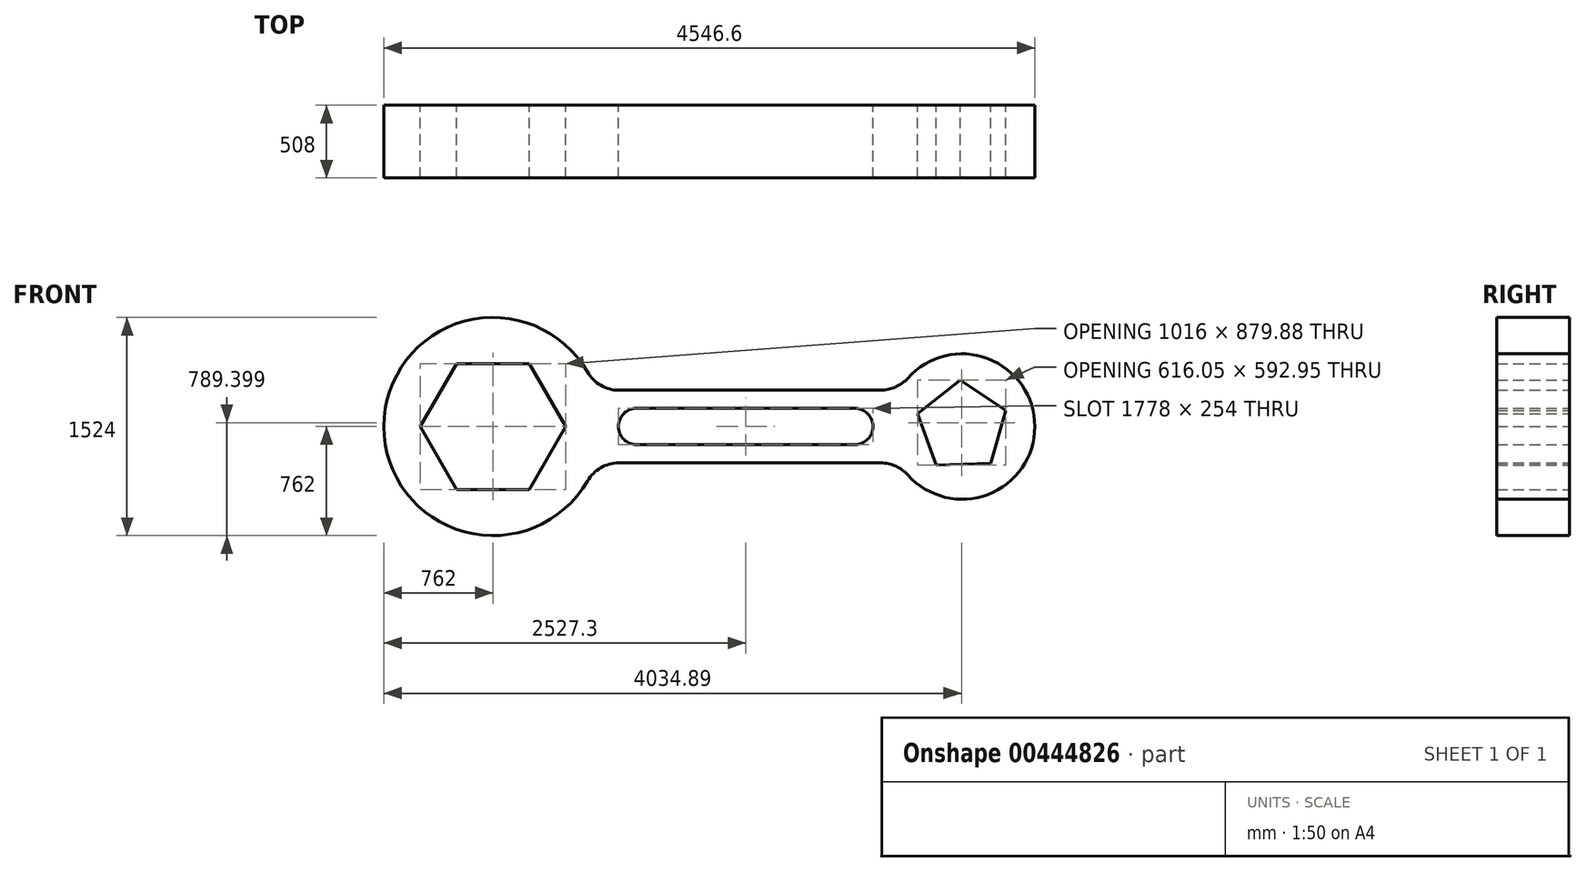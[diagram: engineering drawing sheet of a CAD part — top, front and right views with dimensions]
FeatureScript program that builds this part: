
annotation { "Feature Type Name" : "Feature", "Feature Type Description" : "" }
export const myFeature = defineFeature(function(context is Context, id is Id, definition is map)
    precondition{}
    {
        {
            var Q0;
            Q0=qCreatedBy(makeId("Front.planeOp"),FACE);
            var sketch = newSketch(context, id + "F0", { "sketchPlane" : qUnion([Q0])});
            skCircle(sketch, "E0", {"center": v(0, 0) * mm, "radius": 762 * mm});
            skLineSegment(sketch, "E1.0", {"start": v(-254, 439.94) * mm, "end": v(254, 439.94) * mm});
            skLineSegment(sketch, "E1.1", {"start": v(254, 439.94) * mm, "end": v(508, 0) * mm});
            skLineSegment(sketch, "E1.2", {"start": v(508, 0) * mm, "end": v(254, -439.94) * mm});
            skLineSegment(sketch, "E1.3", {"start": v(254, -439.94) * mm, "end": v(-254, -439.94) * mm});
            skLineSegment(sketch, "E1.4", {"start": v(-254, -439.94) * mm, "end": v(-508, 0) * mm});
            skLineSegment(sketch, "E1.5", {"start": v(-508, 0) * mm, "end": v(-254, 439.94) * mm});
            skPoint(sketch, "E1.0.midPoint", {"position": v(0, 439.94) * mm});
            skCircle(sketch, "E2", {"center": v(3276.6, 0) * mm, "radius": 508 * mm});
            skCircle(sketch, "E3.cCircle", {"center": v(3276.6, 0) * mm, "radius": 262.2 * mm, "construction": true});
            skLineSegment(sketch, "E3.0", {"start": v(2964.87, 88.67) * mm, "end": v(3264.6, 323.88) * mm});
            skLineSegment(sketch, "E3.1", {"start": v(3264.6, 323.88) * mm, "end": v(3580.91, 111.5) * mm});
            skLineSegment(sketch, "E3.2", {"start": v(3580.91, 111.5) * mm, "end": v(3476.68, -254.96) * mm});
            skLineSegment(sketch, "E3.3", {"start": v(3476.68, -254.96) * mm, "end": v(3095.94, -269.08) * mm});
            skLineSegment(sketch, "E3.4", {"start": v(3095.94, -269.08) * mm, "end": v(2964.87, 88.67) * mm});
            skPoint(sketch, "E3.0.midPoint", {"position": v(3114.73, 206.27) * mm});
            skLineSegment(sketch, "E4.0", {"start": v(876.3, 254) * mm, "end": v(2708.64, 254) * mm});
            skLineSegment(sketch, "E5.trimOffspring", {"start": v(2997.35, 0) * mm, "end": v(3276.6, 0) * mm});
            skLineSegment(sketch, "E6", {"start": v(1765.3, 0) * mm, "end": v(1765.3, 254) * mm});
            skArc(sketch, "E7", {"start": v(1003.3, 127) * mm, "mid": v(876.3, 0) * mm, "end": v(1003.3, -127) * mm});
            skArc(sketch, "E8", {"start": v(2527.3, -127) * mm, "mid": v(2654.3, 0) * mm, "end": v(2527.3, 127) * mm});
            skLineSegment(sketch, "E9", {"start": v(1003.3, 127) * mm, "end": v(2527.3, 127) * mm});
            skLineSegment(sketch, "E10", {"start": v(1003.3, -127) * mm, "end": v(2527.3, -127) * mm});
            skArc(sketch, "E11", {"start": v(879.88, -254) * mm, "mid": v(752.88, -288.03) * mm, "end": v(659.91, -381) * mm});
            skLineSegment(sketch, "E12.trimOffspring", {"start": v(879.88, -254) * mm, "end": v(2708.64, -254) * mm});
            skArc(sketch, "E13", {"start": v(659.91, 381) * mm, "mid": v(752.88, 288.03) * mm, "end": v(879.88, 254) * mm});
            skArc(sketch, "E14", {"start": v(2708.64, 254) * mm, "mid": v(2812.33, 276.13) * mm, "end": v(2897.96, 338.67) * mm});
            skArc(sketch, "E15", {"start": v(2897.96, -338.67) * mm, "mid": v(2812.33, -276.13) * mm, "end": v(2708.64, -254) * mm});
            skPoint(sketch, "E16.orphan", {"position": v(762, 0) * mm});
            skPoint(sketch, "E17.trimOffspring.end.orphan", {"position": v(2768.6, 0) * mm});
            skLineSegment(sketch, "E18.trimOffspring", {"start": v(3175.55, 254) * mm, "end": v(3276.6, 254) * mm});
            skLineSegment(sketch, "E19.trimOffspring", {"start": v(3090.42, -254) * mm, "end": v(3276.6, -254) * mm});
            skSolve(sketch);
        }
        {
            var Q0;
            Q0 = qSketchRegion(id + "F0", true);
            extrude(context, id + "F1", {"entities" : qUnion([Q0]), "depth" : 25.4 * mm});
        }
        {
            var Q0;
            Q0 = qSketchRegion(id + "F0", true);
            extrude(context, id + "F2", {"entities" : qUnion([Q0]), "operationType" : NewBodyOperationType.ADD, "depth" : 508 * mm});
        }
    });
